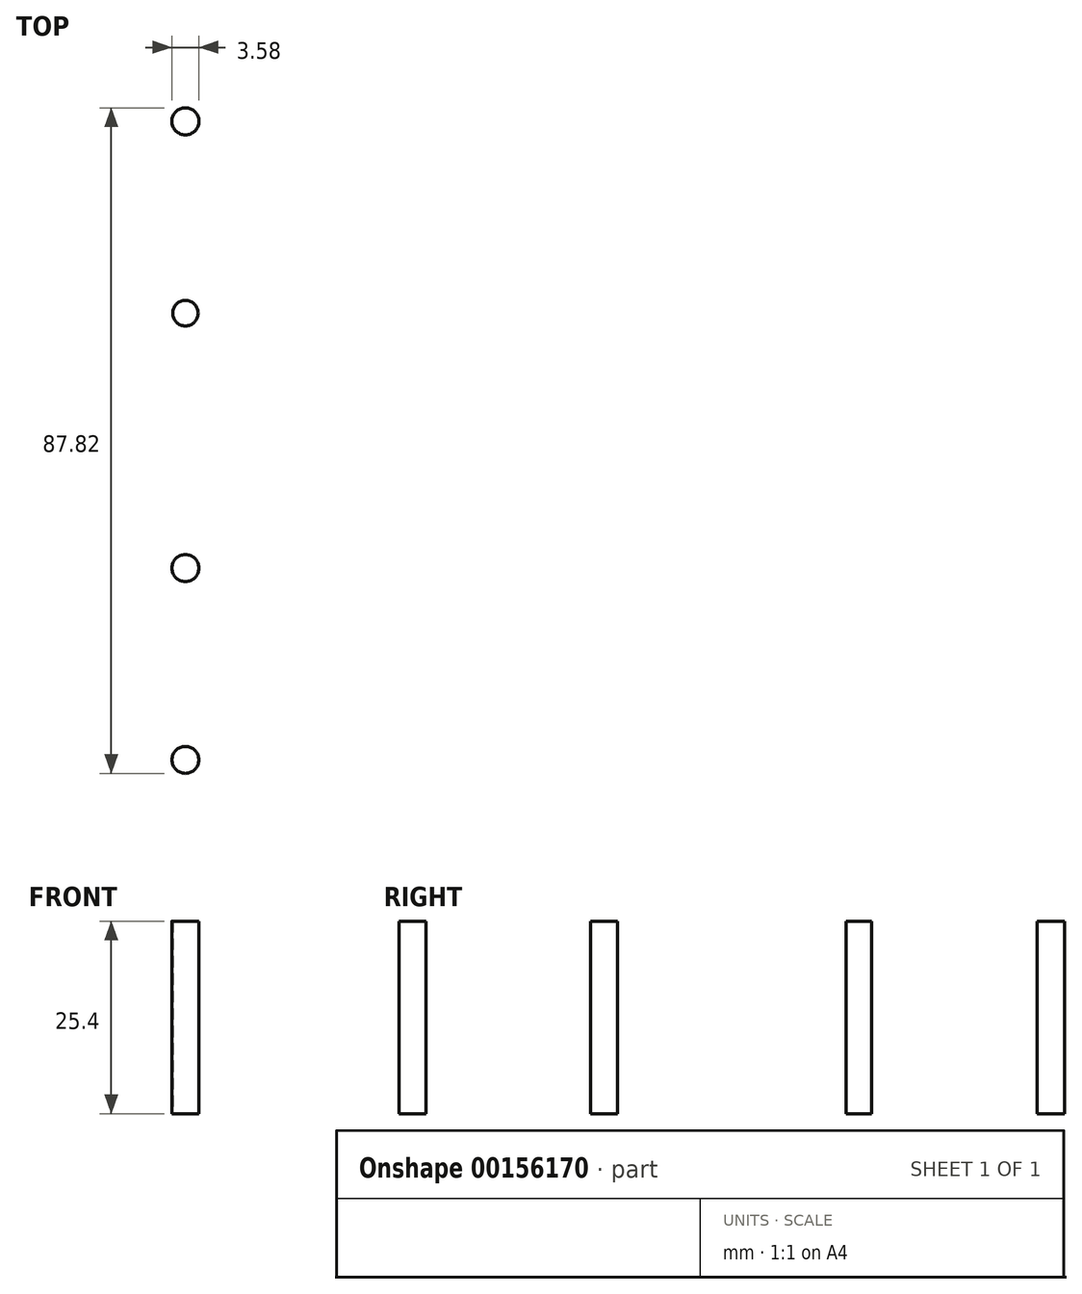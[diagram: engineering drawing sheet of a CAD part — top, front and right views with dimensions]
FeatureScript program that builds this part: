
annotation { "Feature Type Name" : "Feature", "Feature Type Description" : "" }
export const myFeature = defineFeature(function(context is Context, id is Id, definition is map)
    precondition{}
    {
        {
            var Q0;
            Q0=qCreatedBy(makeId("Top.planeOp"),FACE);
            var sketch = newSketch(context, id + "F0", { "sketchPlane" : qUnion([Q0])});
            skLineSegment(sketch, "E0", {"start": v(0, -14.47) * mm, "end": v(0, -9.16) * mm});
            skLineSegment(sketch, "E1", {"start": v(0, -9.16) * mm, "end": v(0, 10.84) * mm});
            skCircle(sketch, "E2", {"center": v(0, -14.47) * mm, "radius": 1.78 * mm});
            skCircle(sketch, "E3", {"center": v(0, 10.84) * mm, "radius": 1.78 * mm});
            skLineSegment(sketch, "E4", {"start": v(0, 10.84) * mm, "end": v(0, 16.15) * mm});
            skLineSegment(sketch, "E5", {"start": v(0, 16.15) * mm, "end": v(0, 72.82) * mm});
            skLineSegment(sketch, "E6", {"start": v(0, 16.15) * mm, "end": v(0, 44.48) * mm});
            skCircle(sketch, "E7", {"center": v(0, 44.48) * mm, "radius": 1.68 * mm});
            skLineSegment(sketch, "E8", {"start": v(0, 44.48) * mm, "end": v(0, 49.8) * mm});
            skLineSegment(sketch, "E9", {"start": v(0, 49.8) * mm, "end": v(0, 69.8) * mm});
            skCircle(sketch, "E10", {"center": v(0, 69.8) * mm, "radius": 1.79 * mm});
            skSolve(sketch);
        }
        {
            var Q0;
            Q0 = qSketchRegion(id + "F0", true);
            extrude(context, id + "F1", {"entities" : qUnion([Q0]), "depth" : 25.4 * mm});
        }
    });
